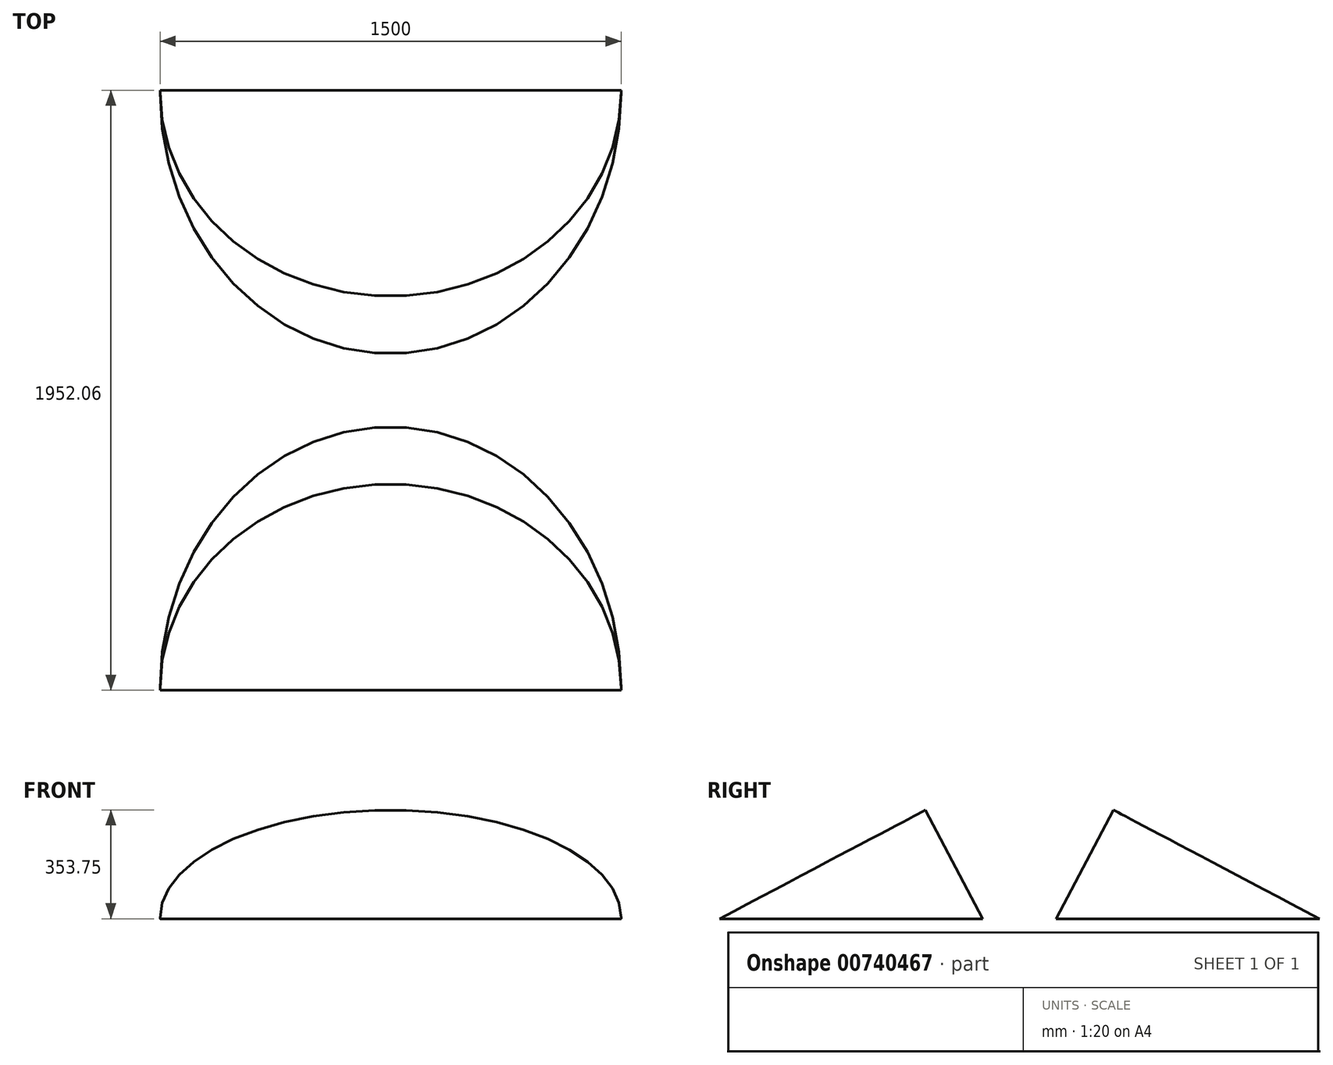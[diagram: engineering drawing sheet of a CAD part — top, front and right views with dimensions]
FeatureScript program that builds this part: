
annotation { "Feature Type Name" : "Feature", "Feature Type Description" : "" }
export const myFeature = defineFeature(function(context is Context, id is Id, definition is map)
    precondition{}
    {
        {
            var Q0;
            Q0=qCreatedBy(makeId("Top.planeOp"),FACE);
            var sketch = newSketch(context, id + "F0", { "sketchPlane" : qUnion([Q0])});
            skCircle(sketch, "E0", {"center": v(0, 0) * mm, "radius": 750 * mm});
            skLineSegment(sketch, "E1", {"start": v(768.01, 750) * mm, "end": v(-848.6, 750) * mm, "construction": true});
            skLineSegment(sketch, "E2.bottom", {"start": v(-912.9, 869.12) * mm, "end": v(912.9, 869.12) * mm});
            skLineSegment(sketch, "E2.top", {"start": v(-912.9, -869.12) * mm, "end": v(912.9, -869.12) * mm});
            skLineSegment(sketch, "E2.left", {"start": v(-912.9, 869.12) * mm, "end": v(-912.9, -869.12) * mm});
            skLineSegment(sketch, "E2.right", {"start": v(912.9, 869.12) * mm, "end": v(912.9, -869.12) * mm});
            skSolve(sketch);
        }
        {
            var Q0;
            Q0=makeQuery(id+"F0.imprint","IMPRINT",FACE,{"disambiguationData":[TD([[makeQuery(id+"F0.imprint","IMPRINT",EDGE,{"derivedFrom":sQuery(id+"F0.wireOp",EDGE,"E0")}),1.0]])]});
            extrude(context, id + "F1", {"entities" : qUnion([Q0]), "depth" : 400 * mm, "offsetDistance" : 25 * mm});
        }
        {
            var Q0;
            Q0=makeQuery(id+"F1.opExtrude","SWEPT_BODY",BODY,{"disambiguationData":[OSD([sQuery(id+"F0.wireOp",EDGE,"E0")])]});
            var Q1;
            Q1=sQuery(id+"F0.wireOp",EDGE,"E1");
            transform(context, id + "F2", {"entities" : qUnion([Q0]), "transformType" : TransformType.ROTATION, "transformAxis" : qUnion([Q1]), "angle" : 27.83 * degree, "oppositeDirection" : true, "makeCopy" : false});
        }
        {
            var Q0;
            Q0=makeQuery(id+"F0.imprint","IMPRINT",FACE,{"disambiguationData":[TD([[makeQuery(id+"F0.imprint","IMPRINT",EDGE,{"derivedFrom":sQuery(id+"F0.wireOp",EDGE,"E0")}),1.0]])]});
            var Q1;
            Q1=makeQuery(id+"F0.imprint","IMPRINT",FACE,{"disambiguationData":[TD([[makeQuery(id+"F0.imprint","IMPRINT",EDGE,{"derivedFrom":sQuery(id+"F0.wireOp",EDGE,"E0")}),-1.0]])]});
            extrude(context, id + "F3", {"entities" : qUnion([Q0, Q1]), "operationType" : NewBodyOperationType.REMOVE, "oppositeDirection" : true, "depth" : 1100 * mm, "offsetDistance" : 25 * mm});
        }
        {
            var Q0;
            Q0=sQuery(id+"F0.wireOp",VERTEX,"E2.bottom.end");
            var Q1;
            Q1=sQuery(id+"F0.wireOp",EDGE,"E2.right");
            cPlane(context, id + "F4", {"entities" : qUnion([Q0, Q1]), "cplaneType" : CPlaneType.LINE_POINT, "offset" : 25 * mm, "width" : 150 * mm, "height" : 150 * mm});
        }
        {
            var Q0;
            Q0=makeQuery(id+"F1.opExtrude","SWEPT_BODY",BODY,{"disambiguationData":[OSD([sQuery(id+"F0.wireOp",EDGE,"E0")])]});
            var Q1;
            Q1=qCreatedBy(id+"F4.planeOp",FACE);
            mirror(context, id + "F5", {"operationType" : NewBodyOperationType.ADD, "entities" : qUnion([Q0]), "mirrorPlane" : qUnion([Q1])});
        }
    });
